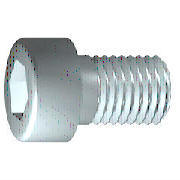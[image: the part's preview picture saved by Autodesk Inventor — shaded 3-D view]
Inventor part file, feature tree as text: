
AUTODESK INVENTOR PART (.ipt)
format: ipt  version: 2020 (Build 240168000, 168)  size: 192,000 bytes
history: native  units: mm (DEFAULTED — no unit token found)
features: sketch x2, other x1, extrude x1, plane x1, fillet x1
ambient origin geometry x7: Origin, YZ Plane, XY Plane, X Axis, Y Axis, Z Axis, Center Point
bodies: Solid1 (feature_tree)
feature tree (6):
  other  "Bryła"
  extrude  "Szczelina"  Depth=10.5mm
  plane  "Work Plane1"
  fillet  "Fillet2"  Radius=0.306825mm
  sketch  "Szkic1"
  sketch  "Szkic2"
